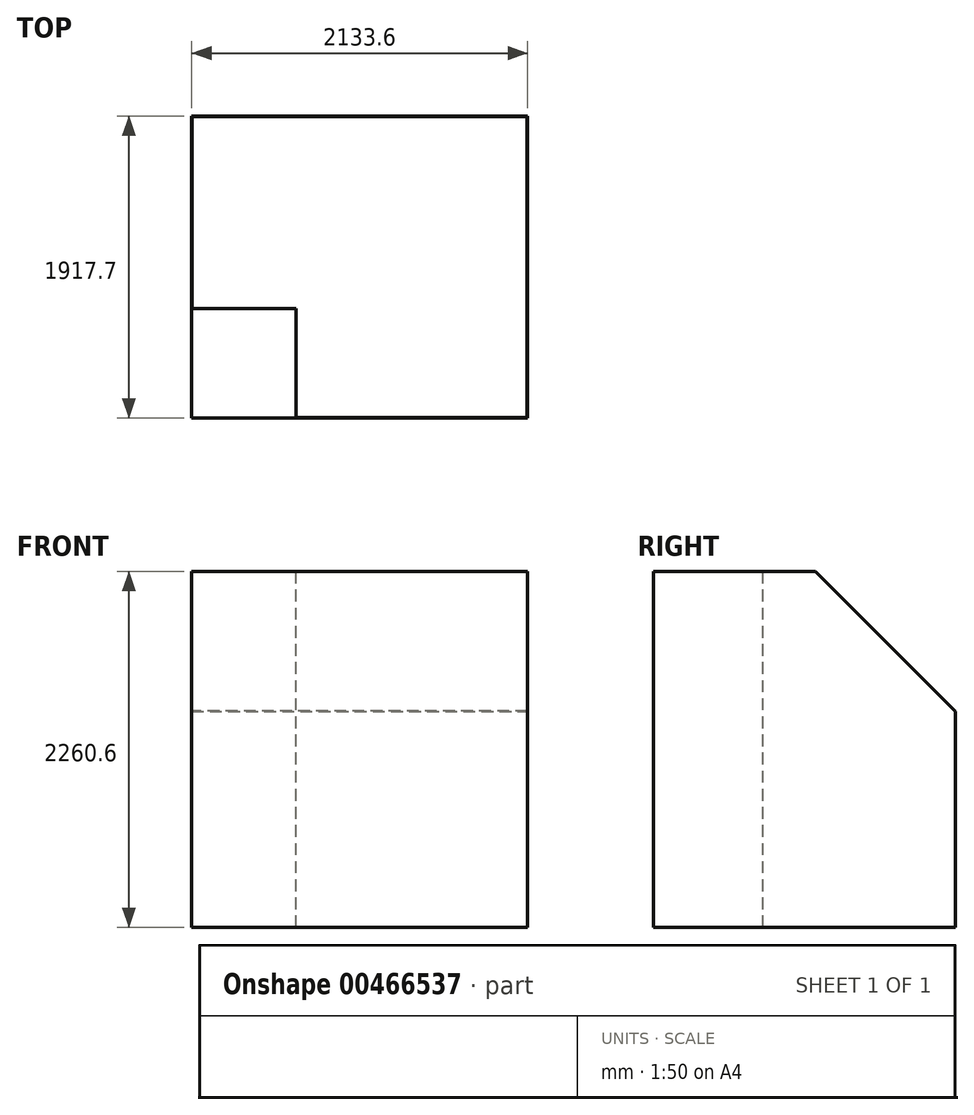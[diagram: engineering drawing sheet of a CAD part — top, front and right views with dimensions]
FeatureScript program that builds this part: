
annotation { "Feature Type Name" : "Feature", "Feature Type Description" : "" }
export const myFeature = defineFeature(function(context is Context, id is Id, definition is map)
    precondition{}
    {
        {
            var Q0;
            Q0=qCreatedBy(makeId("Top.planeOp"),FACE);
            var sketch = newSketch(context, id + "F0", { "sketchPlane" : qUnion([Q0])});
            skLineSegment(sketch, "E0", {"start": v(0, 0) * mm, "end": v(2133.6, 0) * mm});
            skLineSegment(sketch, "E1", {"start": v(2133.6, 0) * mm, "end": v(2133.6, 1917.7) * mm});
            skLineSegment(sketch, "E2", {"start": v(2133.6, 1917.7) * mm, "end": v(0, 1917.7) * mm});
            skLineSegment(sketch, "E3", {"start": v(0, 1917.7) * mm, "end": v(0, 0) * mm});
            skSolve(sketch);
        }
        {
            var Q0;
            Q0=qSketchRegion(id+"F0",true);
            extrude(context, id + "F1", {"entities" : qUnion([Q0]), "depth" : 2260.6 * mm});
        }
        {
            var Q0;
            Q0=makeQuery(id+"F1.opExtrude","CAP_FACE",FACE,{"disambiguationData":[OSD([sQuery(id+"F0.wireOp",EDGE,"E0"),sQuery(id+"F0.wireOp",EDGE,"E1"),sQuery(id+"F0.wireOp",EDGE,"E2"),sQuery(id+"F0.wireOp",EDGE,"E3")])],"isStart":false});
            var sketch = newSketch(context, id + "F2", { "sketchPlane" : qUnion([Q0])});
            skLineSegment(sketch, "E4.bottom", {"start": v(2130.43, 1914.53) * mm, "end": v(1139.82, 1914.53) * mm});
            skLineSegment(sketch, "E4.top", {"start": v(2130.43, 695.32) * mm, "end": v(1139.83, 695.32) * mm});
            skLineSegment(sketch, "E4.right", {"start": v(1139.82, 1914.53) * mm, "end": v(1139.83, 695.32) * mm});
            skLineSegment(sketch, "E5.bottom", {"start": v(3.18, 1914.52) * mm, "end": v(1019.18, 1914.52) * mm});
            skLineSegment(sketch, "E5.top", {"start": v(3.18, 695.32) * mm, "end": v(1019.18, 695.32) * mm});
            skLineSegment(sketch, "E5.right", {"start": v(1019.18, 1914.53) * mm, "end": v(1019.18, 695.32) * mm});
            skLineSegment(sketch, "E6", {"start": v(3.18, 1914.52) * mm, "end": v(3.18, 695.32) * mm});
            skLineSegment(sketch, "E7", {"start": v(2130.43, 1914.53) * mm, "end": v(2130.43, 695.32) * mm});
            skSolve(sketch);
        }
        {
            var Q0;
            Q0=qSketchRegion(id+"F2",true);
            extrude(context, id + "F3", {"entities" : qUnion([Q0]), "operationType" : NewBodyOperationType.REMOVE, "endBound" : BoundingType.THROUGH_ALL, "oppositeDirection" : true, "depth" : 25.4 * mm});
        }
        {
            var Q0;
            Q0=makeQuery(id+"F1.opExtrude","CAP_FACE",FACE,{"disambiguationData":[OSD([sQuery(id+"F0.wireOp",EDGE,"E0"),sQuery(id+"F0.wireOp",EDGE,"E1"),sQuery(id+"F0.wireOp",EDGE,"E2"),sQuery(id+"F0.wireOp",EDGE,"E3")])],"isStart":false});
            var sketch = newSketch(context, id + "F4", { "sketchPlane" : qUnion([Q0])});
            skLineSegment(sketch, "E8.bottom", {"start": v(663.58, 460.38) * mm, "end": v(2009.78, 460.38) * mm});
            skLineSegment(sketch, "E8.top", {"start": v(663.58, 3.18) * mm, "end": v(2009.78, 3.18) * mm});
            skLineSegment(sketch, "E8.left", {"start": v(663.58, 460.37) * mm, "end": v(663.58, 3.18) * mm});
            skLineSegment(sketch, "E8.right", {"start": v(2009.78, 460.38) * mm, "end": v(2009.78, 3.18) * mm});
            skLineSegment(sketch, "E9", {"start": v(1019.18, 695.32) * mm, "end": v(1139.83, 695.32) * mm, "construction": true});
            skLineSegment(sketch, "E10", {"start": v(2009.78, 460.38) * mm, "end": v(2130.43, 460.38) * mm, "construction": true});
            skSolve(sketch);
        }
        {
            var Q0;
            Q0=qSketchRegion(id+"F4",true);
            extrude(context, id + "F5", {"entities" : qUnion([Q0]), "operationType" : NewBodyOperationType.REMOVE, "endBound" : BoundingType.THROUGH_ALL, "oppositeDirection" : true, "depth" : 25.4 * mm});
        }
        {
            var Q0;
            Q0=makeQuery(id+"F1.opExtrude","SWEPT_FACE",FACE,{"disambiguationData":[OSD([sQuery(id+"F0.wireOp",EDGE,"E1")])]});
            var sketch = newSketch(context, id + "F6", { "sketchPlane" : qUnion([Q0])});
            skLineSegment(sketch, "E11", {"start": v(1917.7, 2260.6) * mm, "end": v(1028.7, 2260.6) * mm});
            skLineSegment(sketch, "E12", {"start": v(1028.7, 2260.6) * mm, "end": v(1917.7, 1371.6) * mm});
            skLineSegment(sketch, "E13", {"start": v(1917.7, 1371.6) * mm, "end": v(1917.7, 2260.6) * mm});
            skSolve(sketch);
        }
        {
            var Q0;
            Q0=qSketchRegion(id+"F6",true);
            extrude(context, id + "F7", {"entities" : qUnion([Q0]), "operationType" : NewBodyOperationType.REMOVE, "endBound" : BoundingType.THROUGH_ALL, "oppositeDirection" : true, "depth" : 25.4 * mm});
        }
        {
            var Q0;
            Q0=makeQuery(id+"F1.opExtrude","CAP_FACE",FACE,{"disambiguationData":[OSD([sQuery(id+"F0.wireOp",EDGE,"E0"),sQuery(id+"F0.wireOp",EDGE,"E1"),sQuery(id+"F0.wireOp",EDGE,"E2"),sQuery(id+"F0.wireOp",EDGE,"E3")])],"isStart":false});
            var sketch = newSketch(context, id + "F8", { "sketchPlane" : qUnion([Q0])});
            skLineSegment(sketch, "E14.bottom", {"start": v(663.58, 460.38) * mm, "end": v(2130.43, 460.38) * mm});
            skLineSegment(sketch, "E14.top", {"start": v(663.58, 695.32) * mm, "end": v(2130.43, 695.32) * mm});
            skLineSegment(sketch, "E14.left", {"start": v(663.58, 460.38) * mm, "end": v(663.58, 695.32) * mm});
            skLineSegment(sketch, "E14.right", {"start": v(2130.43, 460.38) * mm, "end": v(2130.43, 695.32) * mm});
            skSolve(sketch);
        }
        {
            var Q0;
            Q0 = qSketchRegion(id + "F8", true);
            extrude(context, id + "F9", {"entities" : qUnion([Q0]), "operationType" : NewBodyOperationType.REMOVE, "endBound" : BoundingType.THROUGH_ALL, "oppositeDirection" : true, "depth" : 25.4 * mm});
        }
        {
            var Q0;
            Q0=makeQuery(id+"F9.boolean.opBoolean","SPLIT",FACE,{"disambiguationData":[TD([makeQuery(id+"F3.boolean.opBoolean","COPY",FACE,{"derivedFrom":makeQuery(id+"F3.opExtrude","SWEPT_FACE",FACE,{"disambiguationData":[OSD([sQuery(id+"F2.wireOp",EDGE,"E4.right")])]})})])],"derivedFrom":makeQuery(id+"F1.opExtrude","CAP_FACE",FACE,{"disambiguationData":[OSD([sQuery(id+"F0.wireOp",EDGE,"E0"),sQuery(id+"F0.wireOp",EDGE,"E1"),sQuery(id+"F0.wireOp",EDGE,"E2"),sQuery(id+"F0.wireOp",EDGE,"E3")])],"isStart":false})});
            var sketch = newSketch(context, id + "F10", { "sketchPlane" : qUnion([Q0])});
            skLineSegment(sketch, "E15.bottom", {"start": v(1019.18, 695.32) * mm, "end": v(1139.83, 695.32) * mm});
            skLineSegment(sketch, "E15.top", {"start": v(1019.17, 1914.53) * mm, "end": v(1139.82, 1914.53) * mm});
            skLineSegment(sketch, "E15.left", {"start": v(1019.18, 695.32) * mm, "end": v(1019.18, 1914.53) * mm});
            skLineSegment(sketch, "E15.right", {"start": v(1139.83, 695.32) * mm, "end": v(1139.82, 1914.53) * mm});
            skLineSegment(sketch, "E16.bottom", {"start": v(2009.78, 460.38) * mm, "end": v(2130.43, 460.38) * mm});
            skLineSegment(sketch, "E16.top", {"start": v(2009.78, 3.18) * mm, "end": v(2130.43, 3.18) * mm});
            skLineSegment(sketch, "E16.left", {"start": v(2009.78, 460.38) * mm, "end": v(2009.78, 3.18) * mm});
            skLineSegment(sketch, "E16.right", {"start": v(2130.43, 460.38) * mm, "end": v(2130.43, 3.18) * mm});
            skSolve(sketch);
        }
        {
            var Q0;
            Q0 = qSketchRegion(id + "F10", true);
            extrude(context, id + "F11", {"entities" : qUnion([Q0]), "operationType" : NewBodyOperationType.REMOVE, "endBound" : BoundingType.THROUGH_ALL, "oppositeDirection" : true, "depth" : 25.4 * mm});
        }
    });
